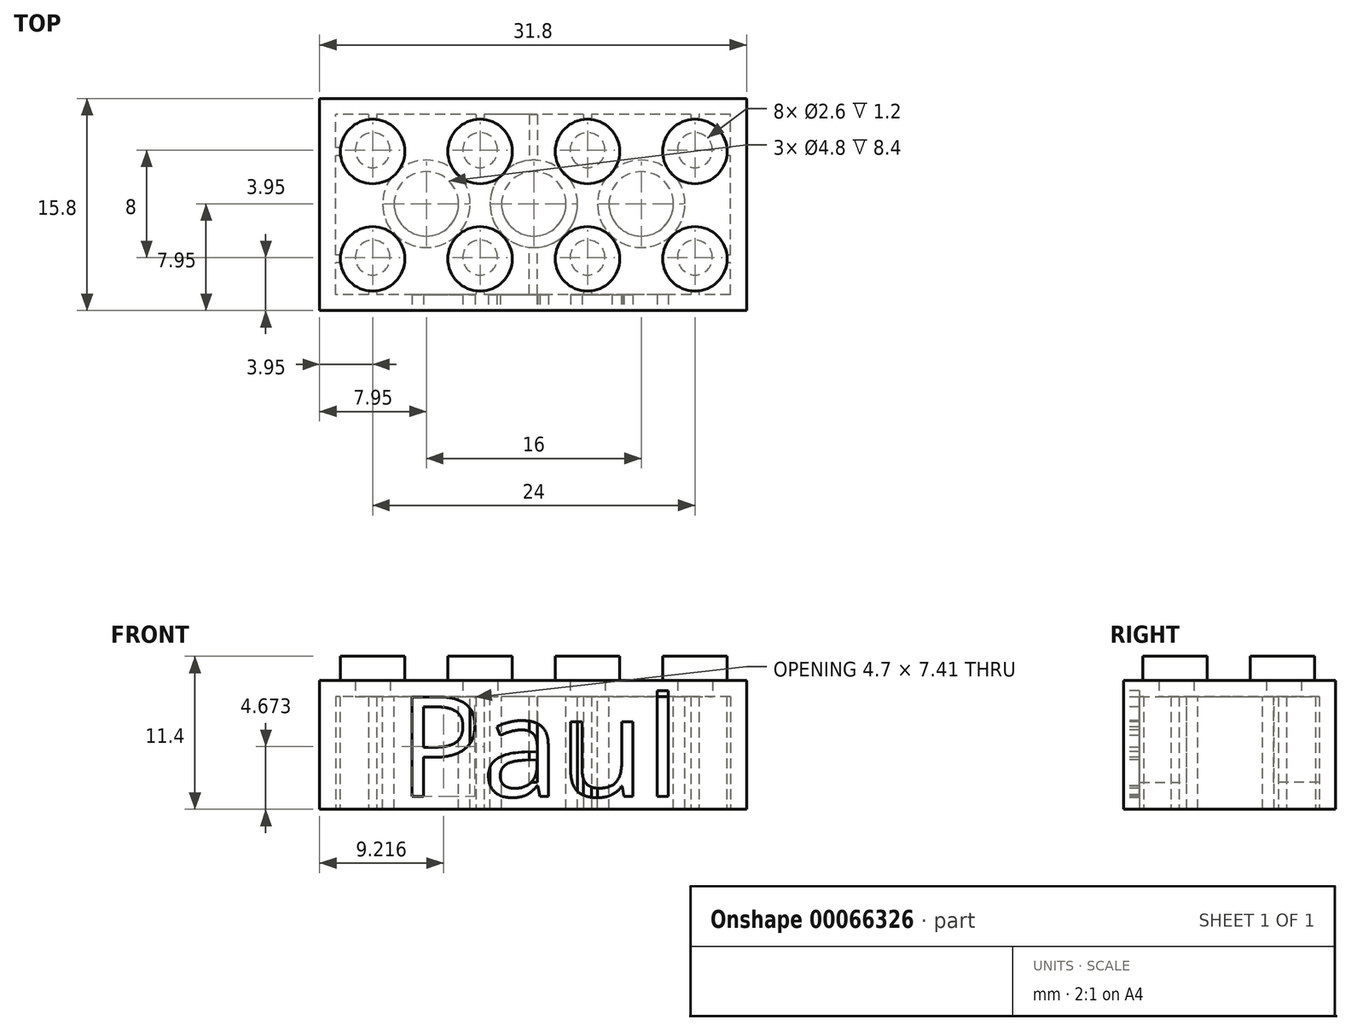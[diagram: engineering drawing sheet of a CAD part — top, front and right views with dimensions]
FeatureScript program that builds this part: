
annotation { "Feature Type Name" : "Feature", "Feature Type Description" : "" }
export const myFeature = defineFeature(function(context is Context, id is Id, definition is map)
    precondition{}
    {
        {
            var Q0;
            Q0=qCreatedBy(makeId("Top.planeOp"),FACE);
            var sketch = newSketch(context, id + "F0", { "sketchPlane" : qUnion([Q0])});
            skLineSegment(sketch, "E0.rect.bottom", {"start": v(15.9, 7.9) * mm, "end": v(-15.9, 7.9) * mm});
            skLineSegment(sketch, "E0.rect.top", {"start": v(15.9, -7.9) * mm, "end": v(-15.9, -7.9) * mm});
            skLineSegment(sketch, "E0.rect.left", {"start": v(15.9, 7.9) * mm, "end": v(15.9, -7.9) * mm});
            skLineSegment(sketch, "E0.rect.right", {"start": v(-15.9, 7.9) * mm, "end": v(-15.9, -7.9) * mm});
            skPoint(sketch, "E0.rect.middle", {"position": v(0, 0) * mm});
            skSolve(sketch);
        }
        {
            var Q0;
            Q0 = qSketchRegion(id + "F0", true);
            extrude(context, id + "F1", {"entities" : qUnion([Q0]), "depth" : 9.6 * mm});
        }
        {
            var Q0;
            Q0=makeQuery(id+"F1.opExtrude","CAP_FACE",FACE,{"disambiguationData":[OSD([sQuery(id+"F0.wireOp",EDGE,"E0.rect.bottom"),sQuery(id+"F0.wireOp",EDGE,"E0.rect.top"),sQuery(id+"F0.wireOp",EDGE,"E0.rect.left"),sQuery(id+"F0.wireOp",EDGE,"E0.rect.right")])],"isStart":true});
            var sketch = newSketch(context, id + "F2", { "sketchPlane" : qUnion([Q0])});
            skLineSegment(sketch, "E1.rect.bottom", {"start": v(14.7, 6.7) * mm, "end": v(-14.7, 6.7) * mm});
            skLineSegment(sketch, "E1.rect.top", {"start": v(14.7, -6.7) * mm, "end": v(-14.7, -6.7) * mm});
            skLineSegment(sketch, "E1.rect.left", {"start": v(14.7, 6.7) * mm, "end": v(14.7, -6.7) * mm});
            skLineSegment(sketch, "E1.rect.right", {"start": v(-14.7, 6.7) * mm, "end": v(-14.7, -6.7) * mm});
            skPoint(sketch, "E1.rect.middle", {"position": v(0, 0) * mm});
            skSolve(sketch);
        }
        {
            var Q0;
            Q0 = qSketchRegion(id + "F2", true);
            extrude(context, id + "F3", {"entities" : qUnion([Q0]), "operationType" : NewBodyOperationType.REMOVE, "oppositeDirection" : true, "depth" : 8.4 * mm});
        }
        {
            var Q0;
            Q0=makeQuery(id+"F1.opExtrude","CAP_FACE",FACE,{"disambiguationData":[OSD([sQuery(id+"F0.wireOp",EDGE,"E0.rect.bottom"),sQuery(id+"F0.wireOp",EDGE,"E0.rect.top"),sQuery(id+"F0.wireOp",EDGE,"E0.rect.left"),sQuery(id+"F0.wireOp",EDGE,"E0.rect.right")])],"isStart":false});
            var sketch = newSketch(context, id + "F4", { "sketchPlane" : qUnion([Q0])});
            skLineSegment(sketch, "E2", {"start": v(-30.2, 0) * mm, "end": v(24.88, 0) * mm, "construction": true});
            skCircle(sketch, "E3", {"center": v(-11.95, 3.95) * mm, "radius": 2.4 * mm});
            skCircle(sketch, "E4.0.1.0", {"center": v(-11.95, -4.05) * mm, "radius": 2.4 * mm});
            skCircle(sketch, "E4.1.0.0", {"center": v(-3.95, 3.95) * mm, "radius": 2.4 * mm});
            skCircle(sketch, "E4.1.1.0", {"center": v(-3.95, -4.05) * mm, "radius": 2.4 * mm});
            skCircle(sketch, "E4.2.0.0", {"center": v(4.05, 3.95) * mm, "radius": 2.4 * mm});
            skCircle(sketch, "E4.2.1.0", {"center": v(4.05, -4.05) * mm, "radius": 2.4 * mm});
            skCircle(sketch, "E4.3.0.0", {"center": v(12.05, 3.95) * mm, "radius": 2.4 * mm});
            skCircle(sketch, "E4.3.1.0", {"center": v(12.05, -4.05) * mm, "radius": 2.4 * mm});
            skLineSegment(sketch, "E4.direction1", {"start": v(-11.95, 3.95) * mm, "end": v(-3.95, 3.95) * mm, "construction": true});
            skLineSegment(sketch, "E4.direction2", {"start": v(-11.95, 3.95) * mm, "end": v(-11.95, -4.05) * mm, "construction": true});
            skSolve(sketch);
        }
        {
            var Q0;
            Q0 = qSketchRegion(id + "F4", true);
            extrude(context, id + "F5", {"entities" : qUnion([Q0]), "operationType" : NewBodyOperationType.ADD, "depth" : 1.8 * mm});
        }
        {
            var Q0;
            Q0=makeQuery(id+"F3.boolean.opBoolean","COPY",FACE,{"derivedFrom":makeQuery(id+"F3.opExtrude","CAP_FACE",FACE,{"disambiguationData":[OSD([sQuery(id+"F2.wireOp",EDGE,"E1.rect.bottom"),sQuery(id+"F2.wireOp",EDGE,"E1.rect.top"),sQuery(id+"F2.wireOp",EDGE,"E1.rect.left"),sQuery(id+"F2.wireOp",EDGE,"E1.rect.right")])],"isStart":false})});
            var sketch = newSketch(context, id + "F6", { "sketchPlane" : qUnion([Q0])});
            skCircle(sketch, "E5", {"center": v(-11.95, 3.95) * mm, "radius": 1.3 * mm});
            skCircle(sketch, "E6.0.1.0", {"center": v(-11.95, -4.05) * mm, "radius": 1.3 * mm});
            skCircle(sketch, "E6.1.0.0", {"center": v(-3.95, 3.95) * mm, "radius": 1.3 * mm});
            skCircle(sketch, "E6.1.1.0", {"center": v(-3.95, -4.05) * mm, "radius": 1.3 * mm});
            skCircle(sketch, "E6.2.0.0", {"center": v(4.05, 3.95) * mm, "radius": 1.3 * mm});
            skCircle(sketch, "E6.2.1.0", {"center": v(4.05, -4.05) * mm, "radius": 1.3 * mm});
            skCircle(sketch, "E6.3.0.0", {"center": v(12.05, 3.95) * mm, "radius": 1.3 * mm});
            skCircle(sketch, "E6.3.1.0", {"center": v(12.05, -4.05) * mm, "radius": 1.3 * mm});
            skLineSegment(sketch, "E6.direction1", {"start": v(-11.95, 3.95) * mm, "end": v(-3.95, 3.95) * mm, "construction": true});
            skLineSegment(sketch, "E6.direction2", {"start": v(-11.95, 3.95) * mm, "end": v(-11.95, -4.05) * mm, "construction": true});
            skSolve(sketch);
        }
        {
            var Q0;
            Q0 = qSketchRegion(id + "F6", true);
            extrude(context, id + "F7", {"entities" : qUnion([Q0]), "operationType" : NewBodyOperationType.REMOVE, "oppositeDirection" : true, "depth" : 1.2 * mm});
        }
        {
            var Q0;
            Q0=makeQuery(id+"F3.boolean.opBoolean","COPY",FACE,{"derivedFrom":makeQuery(id+"F3.opExtrude","CAP_FACE",FACE,{"disambiguationData":[OSD([sQuery(id+"F2.wireOp",EDGE,"E1.rect.bottom"),sQuery(id+"F2.wireOp",EDGE,"E1.rect.top"),sQuery(id+"F2.wireOp",EDGE,"E1.rect.left"),sQuery(id+"F2.wireOp",EDGE,"E1.rect.right")])],"isStart":false})});
            var sketch = newSketch(context, id + "F8", { "sketchPlane" : qUnion([Q0])});
            skLineSegment(sketch, "E7", {"start": v(-11.95, 3.95) * mm, "end": v(-3.95, -4.05) * mm, "construction": true});
            skLineSegment(sketch, "E8", {"start": v(-3.95, 3.95) * mm, "end": v(-11.95, -4.05) * mm, "construction": true});
            skLineSegment(sketch, "E9", {"start": v(4.05, 3.95) * mm, "end": v(-3.95, -4.05) * mm, "construction": true});
            skLineSegment(sketch, "E10", {"start": v(-3.95, 3.95) * mm, "end": v(4.05, -4.05) * mm, "construction": true});
            skLineSegment(sketch, "E11", {"start": v(4.05, 3.95) * mm, "end": v(12.05, -4.05) * mm, "construction": true});
            skLineSegment(sketch, "E12", {"start": v(12.05, 3.95) * mm, "end": v(4.05, -4.05) * mm, "construction": true});
            skCircle(sketch, "E13", {"center": v(-7.95, -0.05) * mm, "radius": 2.4 * mm});
            skCircle(sketch, "E14", {"center": v(-7.95, -0.05) * mm, "radius": 3.25 * mm});
            skCircle(sketch, "E15", {"center": v(0.05, -0.05) * mm, "radius": 2.4 * mm});
            skCircle(sketch, "E16", {"center": v(0.05, -0.05) * mm, "radius": 3.25 * mm});
            skCircle(sketch, "E17", {"center": v(8.05, -0.05) * mm, "radius": 2.4 * mm});
            skCircle(sketch, "E18", {"center": v(8.05, -0.05) * mm, "radius": 3.25 * mm});
            skSolve(sketch);
        }
        {
            var Q0;
            Q0 = qSketchRegion(id + "F8", true);
            var Q1;
            Q1=makeQuery(id+"F1.opExtrude","CAP_FACE",FACE,{"disambiguationData":[OSD([sQuery(id+"F0.wireOp",EDGE,"E0.rect.bottom"),sQuery(id+"F0.wireOp",EDGE,"E0.rect.top"),sQuery(id+"F0.wireOp",EDGE,"E0.rect.left"),sQuery(id+"F0.wireOp",EDGE,"E0.rect.right")])],"isStart":true});
            extrude(context, id + "F9", {"entities" : qUnion([Q0]), "operationType" : NewBodyOperationType.ADD, "endBound" : BoundingType.UP_TO_SURFACE, "endBoundEntityFace" : qUnion([Q1]), "depth" : 25 * mm});
        }
        {
            var Q0;
            Q0=makeQuery(id+"F1.opExtrude","CAP_FACE",FACE,{"disambiguationData":[OSD([sQuery(id+"F0.wireOp",EDGE,"E0.rect.bottom"),sQuery(id+"F0.wireOp",EDGE,"E0.rect.top"),sQuery(id+"F0.wireOp",EDGE,"E0.rect.left"),sQuery(id+"F0.wireOp",EDGE,"E0.rect.right")])],"isStart":true});
            var sketch = newSketch(context, id + "F10", { "sketchPlane" : qUnion([Q0])});
            skLineSegment(sketch, "E19.bottom", {"start": v(-12.25, 6.7) * mm, "end": v(-11.65, 6.7) * mm});
            skLineSegment(sketch, "E19.top", {"start": v(-12.25, 6.4) * mm, "end": v(-11.65, 6.4) * mm});
            skLineSegment(sketch, "E19.left", {"start": v(-12.25, 6.7) * mm, "end": v(-12.25, 6.4) * mm});
            skLineSegment(sketch, "E19.right", {"start": v(-11.65, 6.7) * mm, "end": v(-11.65, 6.4) * mm});
            skLineSegment(sketch, "E20", {"start": v(-11.95, 14.55) * mm, "end": v(-11.95, -3.95) * mm, "construction": true});
            skLineSegment(sketch, "E21.0.1.0", {"start": v(-12.25, -6.7) * mm, "end": v(-11.65, -6.7) * mm});
            skLineSegment(sketch, "E21.0.1.1", {"start": v(-12.25, -6.4) * mm, "end": v(-12.25, -6.7) * mm});
            skLineSegment(sketch, "E21.0.1.2", {"start": v(-12.25, -6.4) * mm, "end": v(-11.65, -6.4) * mm});
            skLineSegment(sketch, "E21.0.1.3", {"start": v(-11.65, -6.4) * mm, "end": v(-11.65, -6.7) * mm});
            skLineSegment(sketch, "E21.1.0.0", {"start": v(-4.25, 6.4) * mm, "end": v(-3.65, 6.4) * mm});
            skLineSegment(sketch, "E21.1.0.1", {"start": v(-4.25, 6.7) * mm, "end": v(-4.25, 6.4) * mm});
            skLineSegment(sketch, "E21.1.0.2", {"start": v(-4.25, 6.7) * mm, "end": v(-3.65, 6.7) * mm});
            skLineSegment(sketch, "E21.1.0.3", {"start": v(-3.65, 6.7) * mm, "end": v(-3.65, 6.4) * mm});
            skLineSegment(sketch, "E21.1.1.0", {"start": v(-4.25, -6.7) * mm, "end": v(-3.65, -6.7) * mm});
            skLineSegment(sketch, "E21.1.1.1", {"start": v(-4.25, -6.4) * mm, "end": v(-4.25, -6.7) * mm});
            skLineSegment(sketch, "E21.1.1.2", {"start": v(-4.25, -6.4) * mm, "end": v(-3.65, -6.4) * mm});
            skLineSegment(sketch, "E21.1.1.3", {"start": v(-3.65, -6.4) * mm, "end": v(-3.65, -6.7) * mm});
            skLineSegment(sketch, "E21.2.0.0", {"start": v(3.75, 6.4) * mm, "end": v(4.35, 6.4) * mm});
            skLineSegment(sketch, "E21.2.0.1", {"start": v(3.75, 6.7) * mm, "end": v(3.75, 6.4) * mm});
            skLineSegment(sketch, "E21.2.0.2", {"start": v(3.75, 6.7) * mm, "end": v(4.35, 6.7) * mm});
            skLineSegment(sketch, "E21.2.0.3", {"start": v(4.35, 6.7) * mm, "end": v(4.35, 6.4) * mm});
            skLineSegment(sketch, "E21.2.1.0", {"start": v(3.75, -6.7) * mm, "end": v(4.35, -6.7) * mm});
            skLineSegment(sketch, "E21.2.1.1", {"start": v(3.75, -6.4) * mm, "end": v(3.75, -6.7) * mm});
            skLineSegment(sketch, "E21.2.1.2", {"start": v(3.75, -6.4) * mm, "end": v(4.35, -6.4) * mm});
            skLineSegment(sketch, "E21.2.1.3", {"start": v(4.35, -6.4) * mm, "end": v(4.35, -6.7) * mm});
            skLineSegment(sketch, "E21.3.0.0", {"start": v(11.75, 6.4) * mm, "end": v(12.35, 6.4) * mm});
            skLineSegment(sketch, "E21.3.0.1", {"start": v(11.75, 6.7) * mm, "end": v(11.75, 6.4) * mm});
            skLineSegment(sketch, "E21.3.0.2", {"start": v(11.75, 6.7) * mm, "end": v(12.35, 6.7) * mm});
            skLineSegment(sketch, "E21.3.0.3", {"start": v(12.35, 6.7) * mm, "end": v(12.35, 6.4) * mm});
            skLineSegment(sketch, "E21.3.1.0", {"start": v(11.75, -6.7) * mm, "end": v(12.35, -6.7) * mm});
            skLineSegment(sketch, "E21.3.1.1", {"start": v(11.75, -6.4) * mm, "end": v(11.75, -6.7) * mm});
            skLineSegment(sketch, "E21.3.1.2", {"start": v(11.75, -6.4) * mm, "end": v(12.35, -6.4) * mm});
            skLineSegment(sketch, "E21.3.1.3", {"start": v(12.35, -6.4) * mm, "end": v(12.35, -6.7) * mm});
            skLineSegment(sketch, "E21.direction1", {"start": v(-12.25, 6.4) * mm, "end": v(-4.25, 6.4) * mm, "construction": true});
            skLineSegment(sketch, "E21.direction2", {"start": v(-12.25, 6.4) * mm, "end": v(-12.25, -6.7) * mm, "construction": true});
            skSolve(sketch);
        }
        {
            var Q0;
            Q0 = qSketchRegion(id + "F10", true);
            var Q1;
            {var subQ0=sQuery(id+"F2.wireOp",EDGE,"E1.rect.bottom");var subQ1=sQuery(id+"F2.wireOp",EDGE,"E1.rect.top");var subQ2=sQuery(id+"F2.wireOp",EDGE,"E1.rect.left");var subQ3=sQuery(id+"F2.wireOp",EDGE,"E1.rect.right");Q1=makeQuery(id+"F9.boolean.opBoolean","SPLIT",FACE,{"disambiguationData":[TD([makeQuery(id+"F3.boolean.opBoolean","COPY",FACE,{"derivedFrom":makeQuery(id+"F3.opExtrude","SWEPT_FACE",FACE,{"disambiguationData":[OSD([subQ0])]})})])],"derivedFrom":makeQuery(id+"F3.boolean.opBoolean","COPY",FACE,{"derivedFrom":makeQuery(id+"F3.opExtrude","CAP_FACE",FACE,{"disambiguationData":[OSD([subQ0,subQ1,subQ2,subQ3])],"isStart":false})})});}
            extrude(context, id + "F11", {"entities" : qUnion([Q0]), "operationType" : NewBodyOperationType.ADD, "endBound" : BoundingType.UP_TO_SURFACE, "oppositeDirection" : true, "endBoundEntityFace" : qUnion([Q1]), "depth" : 25 * mm});
        }
        {
            var Q0;
            Q0=makeQuery(id+"F11.boolean.opBoolean","MERGE",FACE,{"derivedFrom":[makeQuery(id+"F1.opExtrude","CAP_FACE",FACE,{"disambiguationData":[OSD([sQuery(id+"F0.wireOp",EDGE,"E0.rect.bottom"),sQuery(id+"F0.wireOp",EDGE,"E0.rect.top"),sQuery(id+"F0.wireOp",EDGE,"E0.rect.left"),sQuery(id+"F0.wireOp",EDGE,"E0.rect.right")])],"isStart":true}),makeQuery(id+"F11.opExtrude","CAP_FACE",FACE,{"disambiguationData":[OSD([sQuery(id+"F10.wireOp",EDGE,"E19.bottom"),sQuery(id+"F10.wireOp",EDGE,"E19.top"),sQuery(id+"F10.wireOp",EDGE,"E19.left"),sQuery(id+"F10.wireOp",EDGE,"E19.right")])],"isStart":true}),makeQuery(id+"F11.opExtrude","CAP_FACE",FACE,{"disambiguationData":[OSD([sQuery(id+"F10.wireOp",EDGE,"E21.0.1.0"),sQuery(id+"F10.wireOp",EDGE,"E21.0.1.1"),sQuery(id+"F10.wireOp",EDGE,"E21.0.1.2"),sQuery(id+"F10.wireOp",EDGE,"E21.0.1.3")])],"isStart":true}),makeQuery(id+"F11.opExtrude","CAP_FACE",FACE,{"disambiguationData":[OSD([sQuery(id+"F10.wireOp",EDGE,"E21.1.0.0"),sQuery(id+"F10.wireOp",EDGE,"E21.1.0.1"),sQuery(id+"F10.wireOp",EDGE,"E21.1.0.2"),sQuery(id+"F10.wireOp",EDGE,"E21.1.0.3")])],"isStart":true}),makeQuery(id+"F11.opExtrude","CAP_FACE",FACE,{"disambiguationData":[OSD([sQuery(id+"F10.wireOp",EDGE,"E21.1.1.0"),sQuery(id+"F10.wireOp",EDGE,"E21.1.1.1"),sQuery(id+"F10.wireOp",EDGE,"E21.1.1.2"),sQuery(id+"F10.wireOp",EDGE,"E21.1.1.3")])],"isStart":true}),makeQuery(id+"F11.opExtrude","CAP_FACE",FACE,{"disambiguationData":[OSD([sQuery(id+"F10.wireOp",EDGE,"E21.2.0.0"),sQuery(id+"F10.wireOp",EDGE,"E21.2.0.1"),sQuery(id+"F10.wireOp",EDGE,"E21.2.0.2"),sQuery(id+"F10.wireOp",EDGE,"E21.2.0.3")])],"isStart":true}),makeQuery(id+"F11.opExtrude","CAP_FACE",FACE,{"disambiguationData":[OSD([sQuery(id+"F10.wireOp",EDGE,"E21.2.1.0"),sQuery(id+"F10.wireOp",EDGE,"E21.2.1.1"),sQuery(id+"F10.wireOp",EDGE,"E21.2.1.2"),sQuery(id+"F10.wireOp",EDGE,"E21.2.1.3")])],"isStart":true}),makeQuery(id+"F11.opExtrude","CAP_FACE",FACE,{"disambiguationData":[OSD([sQuery(id+"F10.wireOp",EDGE,"E21.3.0.0"),sQuery(id+"F10.wireOp",EDGE,"E21.3.0.1"),sQuery(id+"F10.wireOp",EDGE,"E21.3.0.2"),sQuery(id+"F10.wireOp",EDGE,"E21.3.0.3")])],"isStart":true}),makeQuery(id+"F11.opExtrude","CAP_FACE",FACE,{"disambiguationData":[OSD([sQuery(id+"F10.wireOp",EDGE,"E21.3.1.0"),sQuery(id+"F10.wireOp",EDGE,"E21.3.1.1"),sQuery(id+"F10.wireOp",EDGE,"E21.3.1.2"),sQuery(id+"F10.wireOp",EDGE,"E21.3.1.3")])],"isStart":true})]});
            var sketch = newSketch(context, id + "F12", { "sketchPlane" : qUnion([Q0])});
            skLineSegment(sketch, "E22.bottom", {"start": v(-14.7, 4.35) * mm, "end": v(-14.4, 4.35) * mm});
            skLineSegment(sketch, "E22.top", {"start": v(-14.7, 3.75) * mm, "end": v(-14.4, 3.75) * mm});
            skLineSegment(sketch, "E22.left", {"start": v(-14.7, 4.35) * mm, "end": v(-14.7, 3.75) * mm});
            skLineSegment(sketch, "E22.right", {"start": v(-14.4, 4.35) * mm, "end": v(-14.4, 3.75) * mm});
            skLineSegment(sketch, "E23.0.1.0", {"start": v(-14.7, -3.65) * mm, "end": v(-14.4, -3.65) * mm});
            skLineSegment(sketch, "E23.0.1.1", {"start": v(-14.4, -3.65) * mm, "end": v(-14.4, -4.25) * mm});
            skLineSegment(sketch, "E23.0.1.2", {"start": v(-14.7, -4.25) * mm, "end": v(-14.4, -4.25) * mm});
            skLineSegment(sketch, "E23.0.1.3", {"start": v(-14.7, -3.65) * mm, "end": v(-14.7, -4.25) * mm});
            skLineSegment(sketch, "E23.1.0.0", {"start": v(14.4, 4.35) * mm, "end": v(14.7, 4.35) * mm});
            skLineSegment(sketch, "E23.1.0.1", {"start": v(14.7, 4.35) * mm, "end": v(14.7, 3.75) * mm});
            skLineSegment(sketch, "E23.1.0.2", {"start": v(14.4, 3.75) * mm, "end": v(14.7, 3.75) * mm});
            skLineSegment(sketch, "E23.1.0.3", {"start": v(14.4, 4.35) * mm, "end": v(14.4, 3.75) * mm});
            skLineSegment(sketch, "E23.1.1.0", {"start": v(14.4, -3.65) * mm, "end": v(14.7, -3.65) * mm});
            skLineSegment(sketch, "E23.1.1.1", {"start": v(14.7, -3.65) * mm, "end": v(14.7, -4.25) * mm});
            skLineSegment(sketch, "E23.1.1.2", {"start": v(14.4, -4.25) * mm, "end": v(14.7, -4.25) * mm});
            skLineSegment(sketch, "E23.1.1.3", {"start": v(14.4, -3.65) * mm, "end": v(14.4, -4.25) * mm});
            skLineSegment(sketch, "E23.direction1", {"start": v(-14.7, 4.35) * mm, "end": v(14.4, 4.35) * mm, "construction": true});
            skLineSegment(sketch, "E23.direction2", {"start": v(-14.7, 4.35) * mm, "end": v(-14.7, -3.65) * mm, "construction": true});
            skSolve(sketch);
        }
        {
            var Q0;
            Q0 = qSketchRegion(id + "F12", true);
            var Q1;
            {var subQ0=sQuery(id+"F2.wireOp",EDGE,"E1.rect.bottom");var subQ1=sQuery(id+"F2.wireOp",EDGE,"E1.rect.top");var subQ2=sQuery(id+"F2.wireOp",EDGE,"E1.rect.left");var subQ3=sQuery(id+"F2.wireOp",EDGE,"E1.rect.right");Q1=makeQuery(id+"F9.boolean.opBoolean","SPLIT",FACE,{"disambiguationData":[TD([makeQuery(id+"F3.boolean.opBoolean","COPY",FACE,{"derivedFrom":makeQuery(id+"F3.opExtrude","SWEPT_FACE",FACE,{"disambiguationData":[OSD([subQ0])]})})])],"derivedFrom":makeQuery(id+"F3.boolean.opBoolean","COPY",FACE,{"derivedFrom":makeQuery(id+"F3.opExtrude","CAP_FACE",FACE,{"disambiguationData":[OSD([subQ0,subQ1,subQ2,subQ3])],"isStart":false})})});}
            extrude(context, id + "F13", {"entities" : qUnion([Q0]), "operationType" : NewBodyOperationType.ADD, "endBound" : BoundingType.UP_TO_SURFACE, "oppositeDirection" : true, "endBoundEntityFace" : qUnion([Q1]), "depth" : 25 * mm});
        }
        {
            var Q0;
            {var subQ0=sQuery(id+"F2.wireOp",EDGE,"E1.rect.bottom");var subQ1=sQuery(id+"F2.wireOp",EDGE,"E1.rect.top");var subQ2=sQuery(id+"F2.wireOp",EDGE,"E1.rect.left");var subQ3=sQuery(id+"F2.wireOp",EDGE,"E1.rect.right");Q0=makeQuery(id+"F9.boolean.opBoolean","SPLIT",FACE,{"disambiguationData":[TD([makeQuery(id+"F3.boolean.opBoolean","COPY",FACE,{"derivedFrom":makeQuery(id+"F3.opExtrude","SWEPT_FACE",FACE,{"disambiguationData":[OSD([subQ0])]})})])],"derivedFrom":makeQuery(id+"F3.boolean.opBoolean","COPY",FACE,{"derivedFrom":makeQuery(id+"F3.opExtrude","CAP_FACE",FACE,{"disambiguationData":[OSD([subQ0,subQ1,subQ2,subQ3])],"isStart":false})})});}
            var sketch = newSketch(context, id + "F14", { "sketchPlane" : qUnion([Q0])});
            skLineSegment(sketch, "E24.bottom", {"start": v(-0.3, 6.88) * mm, "end": v(0.3, 6.88) * mm});
            skLineSegment(sketch, "E24.top", {"start": v(-0.3, 2.88) * mm, "end": v(0.3, 2.88) * mm});
            skLineSegment(sketch, "E24.left", {"start": v(-0.3, 6.88) * mm, "end": v(-0.3, 2.88) * mm});
            skLineSegment(sketch, "E24.right", {"start": v(0.3, 6.88) * mm, "end": v(0.3, 2.88) * mm});
            skSolve(sketch);
        }
        {
            var Q0;
            Q0 = qSketchRegion(id + "F14", true);
            extrude(context, id + "F15", {"entities" : qUnion([Q0]), "operationType" : NewBodyOperationType.ADD, "depth" : 6.4 * mm});
        }
        {
            var Q0;
            {var subQ0=sQuery(id+"F2.wireOp",EDGE,"E1.rect.bottom");var subQ1=sQuery(id+"F2.wireOp",EDGE,"E1.rect.top");var subQ2=sQuery(id+"F2.wireOp",EDGE,"E1.rect.left");var subQ3=sQuery(id+"F2.wireOp",EDGE,"E1.rect.right");Q0=makeQuery(id+"F9.boolean.opBoolean","SPLIT",FACE,{"disambiguationData":[TD([makeQuery(id+"F3.boolean.opBoolean","COPY",FACE,{"derivedFrom":makeQuery(id+"F3.opExtrude","SWEPT_FACE",FACE,{"disambiguationData":[OSD([subQ0])]})})])],"derivedFrom":makeQuery(id+"F3.boolean.opBoolean","COPY",FACE,{"derivedFrom":makeQuery(id+"F3.opExtrude","CAP_FACE",FACE,{"disambiguationData":[OSD([subQ0,subQ1,subQ2,subQ3])],"isStart":false})})});}
            var sketch = newSketch(context, id + "F16", { "sketchPlane" : qUnion([Q0])});
            skLineSegment(sketch, "E25.bottom", {"start": v(0.3, -7.1) * mm, "end": v(-0.3, -7.1) * mm});
            skLineSegment(sketch, "E25.top", {"start": v(0.3, -3.1) * mm, "end": v(-0.3, -3.1) * mm});
            skLineSegment(sketch, "E25.left", {"start": v(0.3, -7.1) * mm, "end": v(0.3, -3.1) * mm});
            skLineSegment(sketch, "E25.right", {"start": v(-0.3, -7.1) * mm, "end": v(-0.3, -3.1) * mm});
            skSolve(sketch);
        }
        {
            var Q0;
            Q0 = qSketchRegion(id + "F16", true);
            extrude(context, id + "F17", {"entities" : qUnion([Q0]), "operationType" : NewBodyOperationType.ADD, "depth" : 6.4 * mm});
        }
        {
            var Q0;
            Q0=makeQuery(id+"F1.opExtrude","SWEPT_FACE",FACE,{"disambiguationData":[OSD([sQuery(id+"F0.wireOp",EDGE,"E0.rect.top")])]});
            var sketch = newSketch(context, id + "F18", { "sketchPlane" : qUnion([Q0])});
            skText(sketch, "E26", { "text": "Paul", "fontName": "OpenSans-Regular.ttf"});
            const initialGuessF18  = {"E26": [-0.01005, 0.00097, 1, 0, 0.00747]};
            skSetInitialGuess(sketch, initialGuessF18);
            skSolve(sketch);
        }
        {
            var Q0;
            Q0 = qSketchRegion(id + "F18", true);
            extrude(context, id + "F19", {"entities" : qUnion([Q0]), "operationType" : NewBodyOperationType.REMOVE, "oppositeDirection" : true, "depth" : 1.2 * mm});
        }
    });
